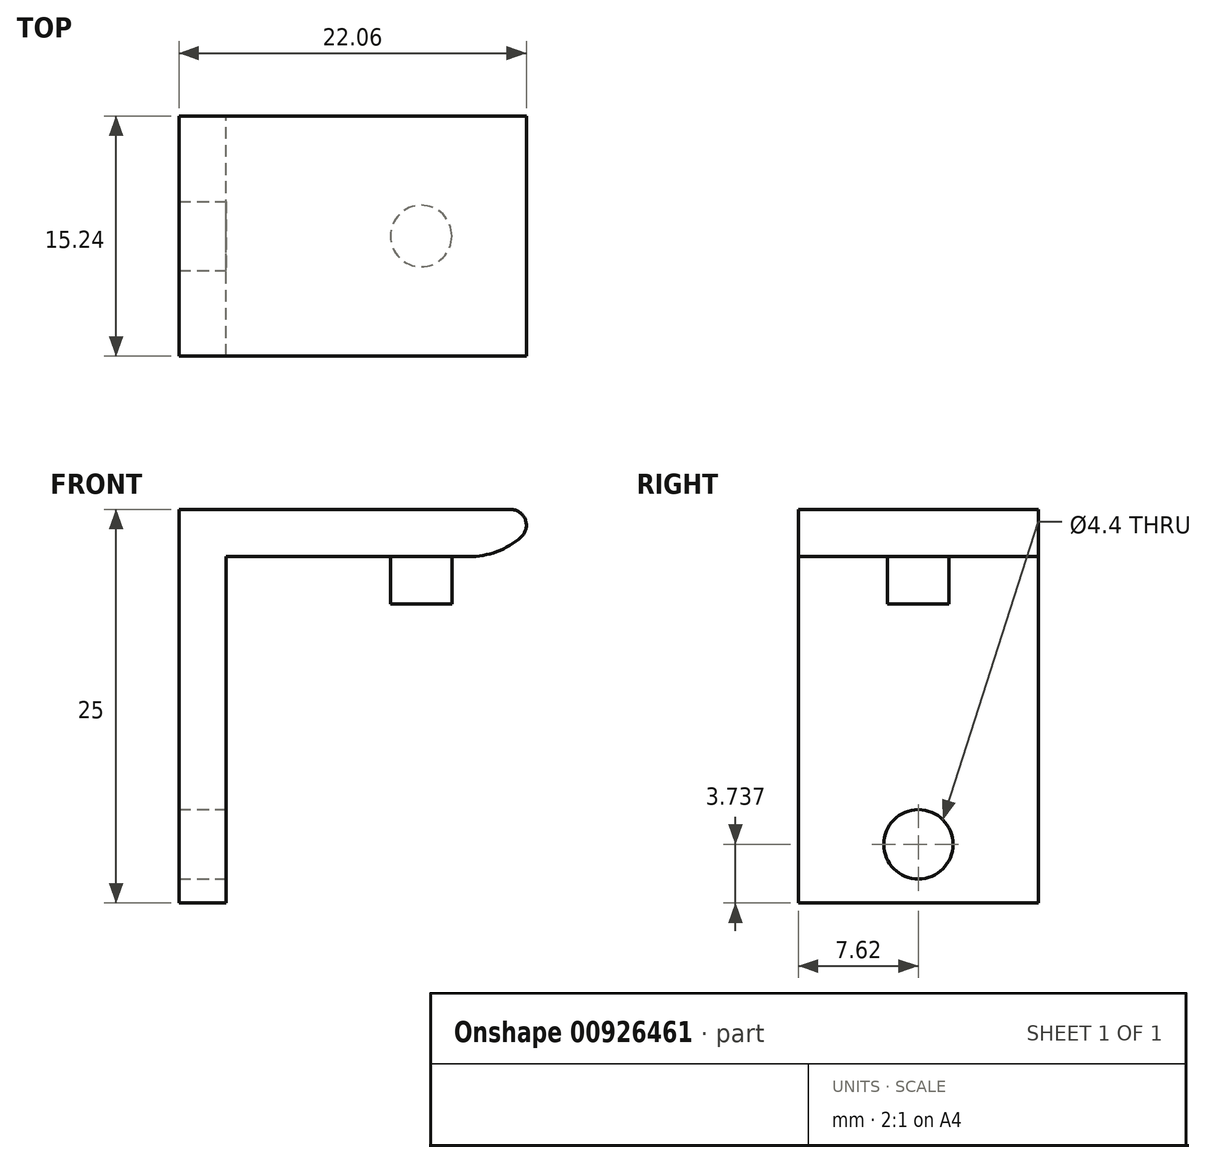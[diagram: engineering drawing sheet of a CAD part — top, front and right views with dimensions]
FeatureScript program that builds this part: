
annotation { "Feature Type Name" : "Feature", "Feature Type Description" : "" }
export const myFeature = defineFeature(function(context is Context, id is Id, definition is map)
    precondition{}
    {
        {
            var Q0;
            Q0=qCreatedBy(makeId("Top.planeOp"),FACE);
            var sketch = newSketch(context, id + "F0", { "sketchPlane" : qUnion([Q0])});
            skLineSegment(sketch, "E0.bottom", {"start": v(-10, -7.62) * mm, "end": v(10, -7.62) * mm});
            skLineSegment(sketch, "E0.top", {"start": v(-10, 7.62) * mm, "end": v(10, 7.62) * mm});
            skLineSegment(sketch, "E0.left", {"start": v(-10, -7.62) * mm, "end": v(-10, 7.62) * mm});
            skLineSegment(sketch, "E0.right", {"start": v(10, -7.62) * mm, "end": v(10, 7.62) * mm});
            skPoint(sketch, "E0.middle", {"position": v(0, 0) * mm});
            skPoint(sketch, "E1", {"position": v(-5.24, 7.62) * mm});
            skLineSegment(sketch, "E2", {"start": v(-5.24, 7.62) * mm, "end": v(-5.24, -7.62) * mm});
            skLineSegment(sketch, "E3", {"start": v(-5.24, -7.62) * mm, "end": v(10, -7.62) * mm});
            skCircle(sketch, "E4", {"center": v(2.38, 0) * mm, "radius": 1.95 * mm});
            skPoint(sketch, "E4.centerSnap0", {"position": v(2.38, -7.62) * mm});
            skSolve(sketch);
        }
        {
            var Q0;
            Q0=makeQuery(id+"F0.imprint","IMPRINT",FACE,{"disambiguationData":[TD([[makeQuery(id+"F0.imprint","IMPRINT",EDGE,{"derivedFrom":sQuery(id+"F0.wireOp",EDGE,"E0.bottom")}),1.0]])]});
            var Q1;
            Q1=makeQuery(id+"F0.imprint","IMPRINT",FACE,{"disambiguationData":[TD([[makeQuery(id+"F0.imprint","IMPRINT",EDGE,{"derivedFrom":sQuery(id+"F0.wireOp",EDGE,"OqzNBpXu-2ITd-4m55-Z498-6EjzGgqgbkyj")}),1.0]])]});
            var Q2;
            {var subQ1=sQuery(id+"F0.wireOp",EDGE,"E0.right");Q2=makeQuery(id+"F0.imprint","IMPRINT",FACE,{"disambiguationData":[TD([[makeQuery(id+"F0.imprint","IMPRINT",EDGE,{"derivedFrom":subQ1}),1.0]])]});}
            var Q3;
            Q3=makeQuery(id+"F0.imprint","IMPRINT",FACE,{"disambiguationData":[TD([[makeQuery(id+"F0.imprint","IMPRINT",EDGE,{"derivedFrom":sQuery(id+"F0.wireOp",EDGE,"E4")}),1.0]])]});
            extrude(context, id + "F1", {"entities" : qUnion([Q0, Q1, Q2, Q3]), "depth" : 3 * mm, "offsetDistance" : 25 * mm});
        }
        {
            var Q0;
            Q0=makeQuery(id+"F0.imprint","IMPRINT",FACE,{"disambiguationData":[TD([[makeQuery(id+"F0.imprint","IMPRINT",EDGE,{"derivedFrom":sQuery(id+"F0.wireOp",EDGE,"E4")}),1.0]])]});
            extrude(context, id + "F2", {"entities" : qUnion([Q0]), "operationType" : NewBodyOperationType.ADD, "oppositeDirection" : true, "depth" : 3 * mm, "offsetDistance" : 25 * mm});
        }
        {
            var Q0;
            Q0=makeQuery(id+"F1.opExtrude","SWEPT_FACE",FACE,{"disambiguationData":[OSD([sQuery(id+"F0.wireOp",EDGE,"E0.left")])]});
            var sketch = newSketch(context, id + "F3", { "sketchPlane" : qUnion([Q0])});
            skLineSegment(sketch, "E5.bottom", {"start": v(-7.62, 3) * mm, "end": v(7.62, 3) * mm});
            skLineSegment(sketch, "E5.top", {"start": v(-7.62, -22) * mm, "end": v(7.62, -22) * mm});
            skLineSegment(sketch, "E5.left", {"start": v(-7.62, 3) * mm, "end": v(-7.62, -22) * mm});
            skLineSegment(sketch, "E5.right", {"start": v(7.62, 3) * mm, "end": v(7.62, -22) * mm});
            skCircle(sketch, "E6", {"center": v(0, -18.26) * mm, "radius": 2.2 * mm});
            skSolve(sketch);
        }
        {
            var Q0;
            {var subQ2=sQuery(id+"F3.wireOp",EDGE,"E5.top");Q0=makeQuery(id+"F3.imprint","IMPRINT",FACE,{"disambiguationData":[TD([[makeQuery(id+"F3.imprint","IMPRINT",EDGE,{"derivedFrom":subQ2}),1.0]])]});}
            var Q1;
            {var subQ0=sQuery(id+"F3.wireOp",EDGE,"E5.bottom");Q1=makeQuery(id+"F3.imprint","IMPRINT",FACE,{"disambiguationData":[TD([[makeQuery(id+"F3.imprint","IMPRINT",EDGE,{"derivedFrom":subQ0}),1.0]])]});}
            extrude(context, id + "F4", {"entities" : qUnion([Q0, Q1]), "operationType" : NewBodyOperationType.ADD, "depth" : 3 * mm, "offsetDistance" : 25 * mm});
        }
        {
            var Q0;
            Q0=makeQuery(id+"F1.opExtrude","CAP_EDGE",EDGE,{"disambiguationData":[OSD([sQuery(id+"F0.wireOp",EDGE,"E0.right")])],"isStart":true});
            fillet(context, id + "F5", {"entities" : qUnion([Q0]), "radius" : 5 * mm, "tangentPropagation" : true, "allowEdgeOverflow" : false});
        }
        {
            var Q0;
            {var subQ0=sQuery(id+"F0.wireOp",EDGE,"E0.right");Q0=makeQuery(id+"F5.opFillet","BLEND_EDGE",EDGE,{"blendedFrom":[makeQuery(id+"F1.opExtrude","CAP_EDGE",EDGE,{"disambiguationData":[OSD([subQ0])],"isStart":true}),makeQuery(id+"F4.boolean.opBoolean","MERGE",FACE,{"derivedFrom":[makeQuery(id+"F1.opExtrude","CAP_FACE",FACE,{"disambiguationData":[OSD([sQuery(id+"F0.wireOp",EDGE,"E0.bottom"),sQuery(id+"F0.wireOp",EDGE,"E0.top"),sQuery(id+"F0.wireOp",EDGE,"E0.left"),subQ0])],"isStart":false}),makeQuery(id+"F4.opExtrude","SWEPT_FACE",FACE,{"disambiguationData":[OSD([sQuery(id+"F3.wireOp",EDGE,"E5.bottom")])]})]})],"blendedInto":[makeQuery(id+"F4.boolean.opBoolean","MERGE",FACE,{"derivedFrom":[makeQuery(id+"F1.opExtrude","CAP_FACE",FACE,{"disambiguationData":[OSD([sQuery(id+"F0.wireOp",EDGE,"E0.bottom"),sQuery(id+"F0.wireOp",EDGE,"E0.top"),sQuery(id+"F0.wireOp",EDGE,"E0.left"),subQ0])],"isStart":false}),makeQuery(id+"F4.opExtrude","SWEPT_FACE",FACE,{"disambiguationData":[OSD([sQuery(id+"F3.wireOp",EDGE,"E5.bottom")])]})]})]});}
            fillet(context, id + "F6", {"entities" : qUnion([Q0]), "radius" : 1 * mm, "tangentPropagation" : true, "allowEdgeOverflow" : false});
        }
    });
